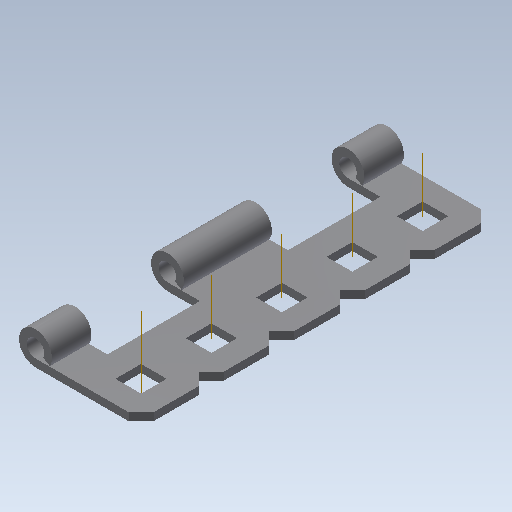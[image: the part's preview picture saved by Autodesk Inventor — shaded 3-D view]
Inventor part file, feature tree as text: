
AUTODESK INVENTOR PART (.ipt)
format: ipt  version: 2020 (Build 240168000, 168)  size: 173,568 bytes
history: native  units: in
note: dims shown in document units (in); Inventor stores cm internally (conversion verified against a paired STEP export)
features: other x8, pattern_linear x1, imported_body x1
ambient origin geometry x8: Origin, YZ Plane, XZ Plane, XY Plane, X Axis, Y Axis, Z Axis, Center Point
bodies: Body1 (feature_tree)
feature tree (10):
  other  "Cut-Extrude3"
  other  "Hinge Plate"
  other  "axis"
  pattern_linear  "Rectangular Pattern1"  Count1=5 Spacing1=0.5in
  imported_body  "Base1"
  other  "Work Point1"
  other  "Work Axis2"
  other  "Work Axis3"
  other  "Work Axis4"
  other  "Work Axis5"
